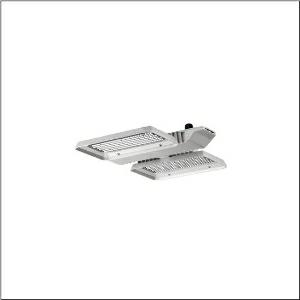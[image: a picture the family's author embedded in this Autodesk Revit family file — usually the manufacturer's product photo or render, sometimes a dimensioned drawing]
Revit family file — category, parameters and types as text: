
# Revit family: highbay_11_51hlasd14fga
name_source: partatom
category: Lighting Fixtures
units: mm (PartAtom-declared; Revit-internal decimal feet)

## family parameters
Cut with Voids When Loaded = No
Host = Face
Light Source = No
Part Type = Normal
Room Calculation Point = No
Round Connector Dimension = Use Diameter
Shared = No

## types (1)
- --- (1 x LED, 14400 lm, 81.3 W, 4000K)
    Apparent Load = 81 VA
    CIE Flux Codes = 89 96 99 100 100
    Color Rendering = 80
    Color Temperature = 4000K
    Default Elevation = 1800 mm
    Description = Highbay 11, LED high bay luminaire, primary light control with lens, of PMMA, light emission: direct distribution, primary light characteristic: symmetric, installation type: suspended mounting, for 1x 2 x LED rated luminous flux: 14.400 lm, light colour: 840, colour temperature: 4000K, control gear: ECG DALI, with terminal, 5-pole, max. 2.5mm², mains connection: 230..240V, AC, 50/60Hz, rated input power: 81W, LED unit, of diecast aluminium, unplated, bead blasted, silver, length: 470 mm, width: 500 mm, height: 65mm, housing, of diecast aluminium, uncoated, bead blasted, silver, protection rating (complete): IP20, insulation class (complete): insulation class I (protective earthing), certification: CE, ENEC, VDE, protection symbol: D, ball protection: ball impact resistant according to DIN VDE 0710 part 13 (with chain suspension), permissible ambient temperature for indoor applications: -35..+55°C, corresponds to IFS (International Featured Standards) requirements for safety and quality in the food industry, reducing of maximum allowable ambient temperature of 5°C with ceiling mounting, packaging unit: 1 piece
    Height = 95 mm
    Lamp = 1 x LED
    Lamp Light Flux = 14400 lm
    Lamp Power = 81.3 W
    Lamp count = 1
    Length = 468 mm
    Luminous efficacy = 177 lm/W
    Manufacturer = Siteco
    ModVariant = No
    Model = 51HLASD14FGA
    Mounting Place = Ceiling
    Mounting Type = Pendant
    Number of Poles = 1
    OnlyDefault = Yes
    Power Factor = 1
    Product Name = Highbay 11
    Product group = LED high bay luminaire
    ProductGroupID = 903
    Protection Class = Protection class I
    Protection Degree = IP 20
    RLX_Detail_Level = 1
    RlxData = <blob elided: 53693 chars, md5=8294d427>
    Socket = socket
    Standby Power = 0 W
    System Light Flux = 14400 lm
    System Power = 81 W
    Type Comments = factory setting: luminous flux: 100 % | dim-lin: 254 | 460 mA
    Type Image = l_1006019.jpg
    URL = http://relux.com
    VarID = @adj_137483
    Voltage = 0 V
    Weight = 0.00 kg
    Width = 501 mm

## geometry (parser evidence)
native form markers: Blend x4, Sweep x14
no freeform markers — native parametric forms only
